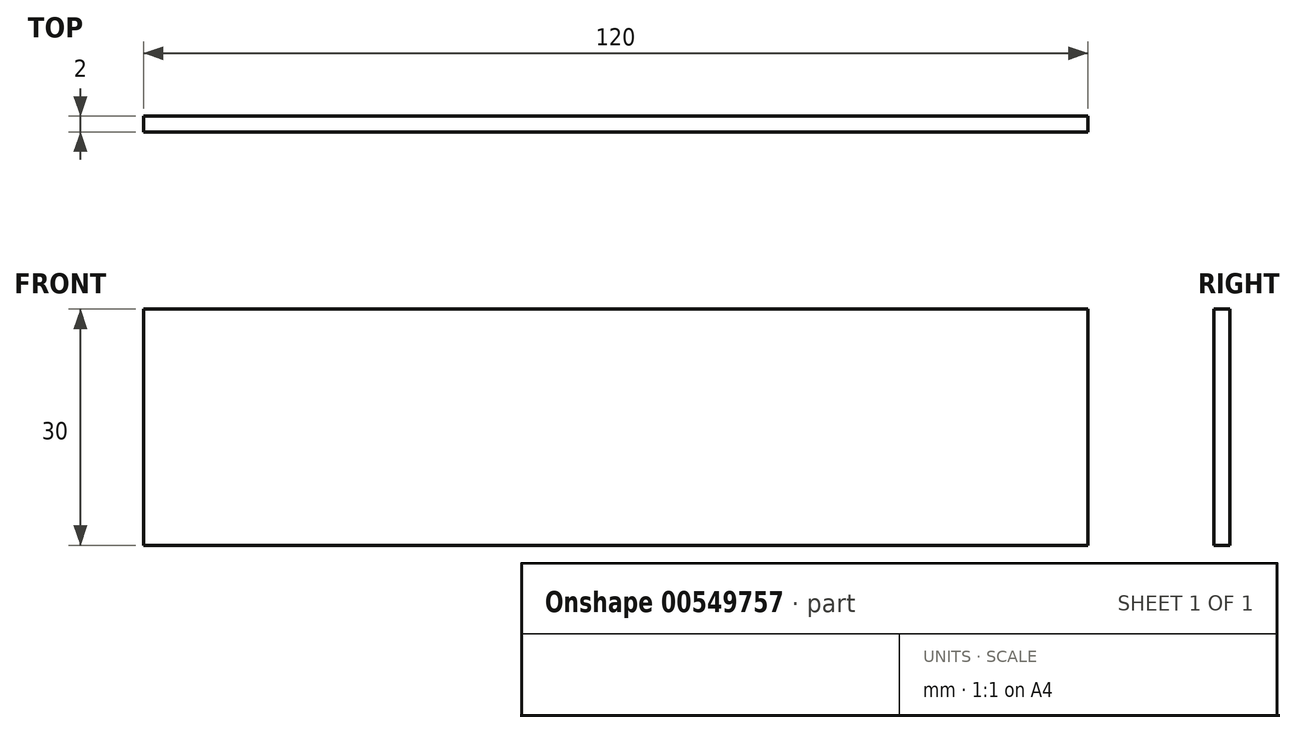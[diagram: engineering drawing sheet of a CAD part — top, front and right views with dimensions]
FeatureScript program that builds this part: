
annotation { "Feature Type Name" : "Feature", "Feature Type Description" : "" }
export const myFeature = defineFeature(function(context is Context, id is Id, definition is map)
    precondition{}
    {
        {
            var Q0;
            Q0=qCreatedBy(makeId("Front.planeOp"),FACE);
            var sketch = newSketch(context, id + "F0", { "sketchPlane" : qUnion([Q0])});
            skLineSegment(sketch, "E0.bottom", {"start": v(0, 0) * mm, "end": v(120, 0) * mm});
            skLineSegment(sketch, "E0.top", {"start": v(0, 30) * mm, "end": v(120, 30) * mm});
            skLineSegment(sketch, "E0.left", {"start": v(0, 0) * mm, "end": v(0, 30) * mm});
            skLineSegment(sketch, "E0.right", {"start": v(120, 0) * mm, "end": v(120, 30) * mm});
            skSolve(sketch);
        }
        {
            var Q0;
            Q0=makeQuery(id+"F0.imprint","IMPRINT",FACE,{"disambiguationData":[TD([[makeQuery(id+"F0.imprint","IMPRINT",EDGE,{"derivedFrom":sQuery(id+"F0.wireOp",EDGE,"E0.bottom")}),1.0]])]});
            extrude(context, id + "F1", {"entities" : qUnion([Q0]), "depth" : 2 * mm, "offsetDistance" : 25 * mm});
        }
    });
